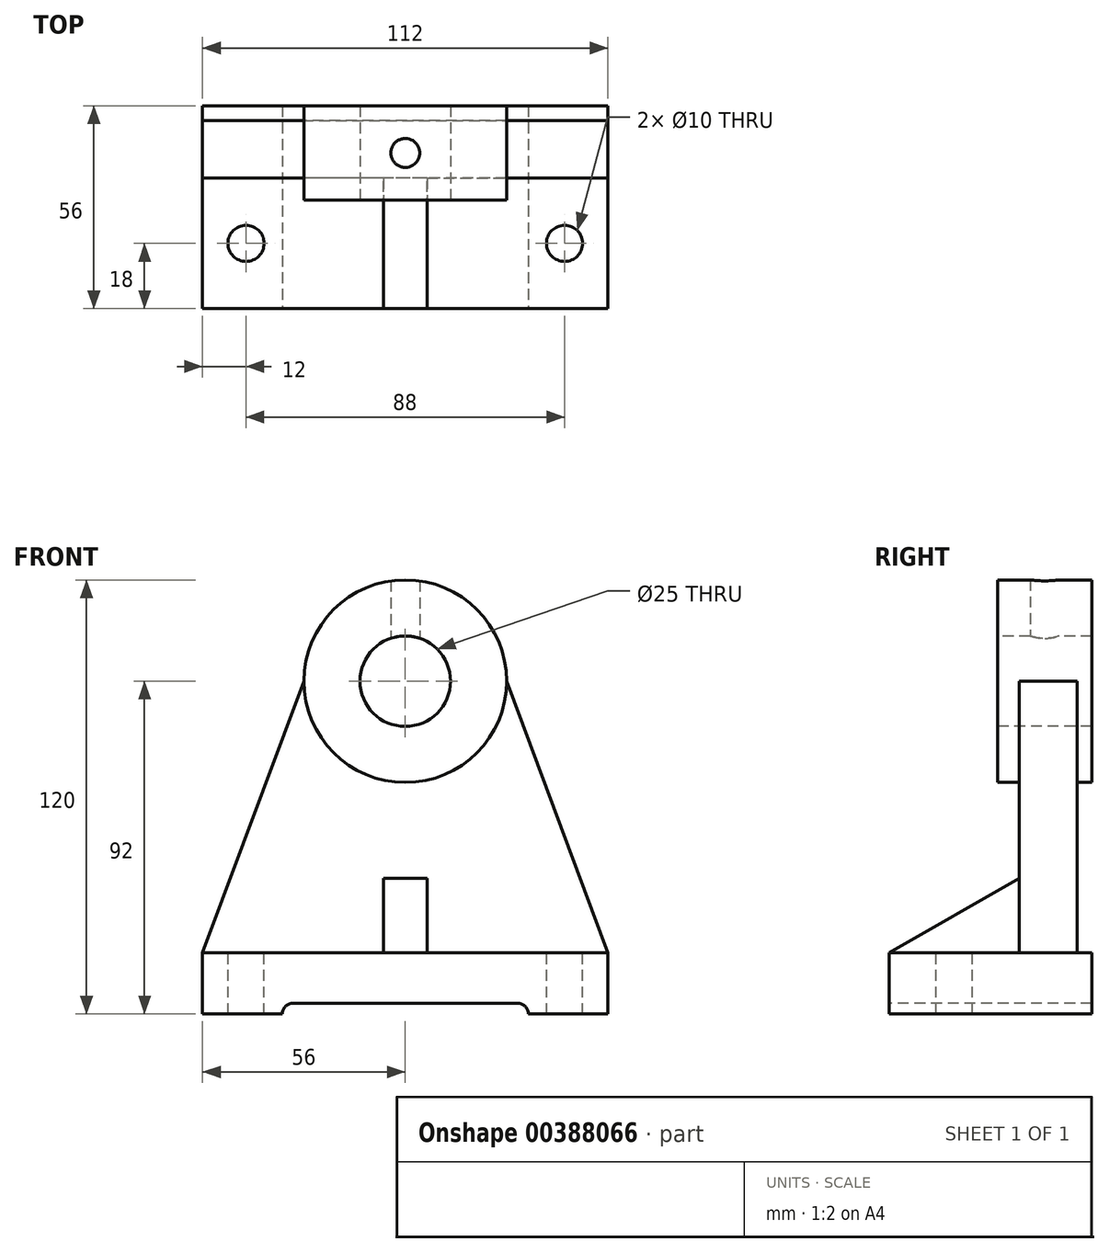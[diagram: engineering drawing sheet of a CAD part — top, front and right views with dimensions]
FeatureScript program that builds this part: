
annotation { "Feature Type Name" : "Feature", "Feature Type Description" : "" }
export const myFeature = defineFeature(function(context is Context, id is Id, definition is map)
    precondition{}
    {
        {
            var Q0;
            Q0=qCreatedBy(makeId("Right.planeOp"),FACE);
            var sketch = newSketch(context, id + "F0", { "sketchPlane" : qUnion([Q0])});
            skLineSegment(sketch, "E0", {"start": v(0, 0) * mm, "end": v(0, 49) * mm});
            skLineSegment(sketch, "E1", {"start": v(0, 0) * mm, "end": v(-56, 0) * mm});
            skLineSegment(sketch, "E2", {"start": v(-56, 0) * mm, "end": v(-56, 17) * mm});
            skLineSegment(sketch, "E3", {"start": v(-20, 37.57) * mm, "end": v(-56, 17) * mm});
            skLineSegment(sketch, "E4", {"start": v(0, 0) * mm, "end": v(0, 92) * mm});
            skLineSegment(sketch, "E5", {"start": v(0, 92) * mm, "end": v(-20, 92) * mm});
            skLineSegment(sketch, "E6", {"start": v(-20, 92) * mm, "end": v(-20, 37.57) * mm});
            skSolve(sketch);
        }
        {
            var Q0;
            Q0 = qSketchRegion(id + "F0", true);
            extrude(context, id + "F1", {"entities" : qUnion([Q0]), "depth" : 112 * mm});
        }
        {
            var Q0;
            Q0=makeQuery(id+"F1.opExtrude","CAP_FACE",FACE,{"disambiguationData":[OSD([sQuery(id+"F0.wireOp",EDGE,"E1"),sQuery(id+"F0.wireOp",EDGE,"E2"),sQuery(id+"F0.wireOp",EDGE,"E3"),sQuery(id+"F0.wireOp",EDGE,"E4"),sQuery(id+"F0.wireOp",EDGE,"E5"),sQuery(id+"F0.wireOp",EDGE,"E6")])],"isStart":false});
            var sketch = newSketch(context, id + "F2", { "sketchPlane" : qUnion([Q0])});
            skPoint(sketch, "E7.start.orphan", {"position": v(0, 17) * mm});
            skLineSegment(sketch, "E8", {"start": v(-4, 17) * mm, "end": v(0, 17) * mm});
            skLineSegment(sketch, "E9", {"start": v(-4, 17) * mm, "end": v(-4, 92) * mm});
            skSolve(sketch);
        }
        {
            var Q0;
            Q0 = qSketchRegion(id + "F2", true);
            var Q1;
            {var subQ0=sQuery(id+"F2.wireOp",EDGE,"E7");Q1=makeQuery(id+"F2.imprint","IMPRINT",FACE,{"disambiguationData":[TD([[makeQuery(id+"F2.imprint","IMPRINT",EDGE,{"derivedFrom":subQ0}),-1.0]])]});}
            var Q2;
            {var subQ0=sQuery(id+"F2.wireOp",EDGE,"E8");Q2=makeQuery(id+"F2.imprint","IMPRINT",FACE,{"disambiguationData":[TD([[makeQuery(id+"F2.imprint","IMPRINT",EDGE,{"derivedFrom":subQ0}),1.0]])]});}
            extrude(context, id + "F3", {"entities" : qUnion([Q0, Q1, Q2]), "operationType" : NewBodyOperationType.REMOVE, "endBound" : BoundingType.THROUGH_ALL, "oppositeDirection" : true, "depth" : 25 * mm});
        }
        {
            var Q0;
            Q0=makeQuery(id+"F1.opExtrude","CAP_FACE",FACE,{"disambiguationData":[OSD([sQuery(id+"F0.wireOp",EDGE,"E1"),sQuery(id+"F0.wireOp",EDGE,"E2"),sQuery(id+"F0.wireOp",EDGE,"E3"),sQuery(id+"F0.wireOp",EDGE,"E4"),sQuery(id+"F0.wireOp",EDGE,"E5"),sQuery(id+"F0.wireOp",EDGE,"E6")])],"isStart":false});
            var sketch = newSketch(context, id + "F4", { "sketchPlane" : qUnion([Q0])});
            skLineSegment(sketch, "E10", {"start": v(-56, 17) * mm, "end": v(-20, 17) * mm});
            skLineSegment(sketch, "E11", {"start": v(-20, 17) * mm, "end": v(-20, 37.57) * mm});
            skSolve(sketch);
        }
        {
            var Q0;
            Q0 = qSketchRegion(id + "F4", true);
            var Q1;
            Q1=makeQuery(id+"F4.imprint","IMPRINT",FACE,{"disambiguationData":[TD([[makeQuery(id+"F4.imprint","IMPRINT",EDGE,{"derivedFrom":sQuery(id+"F4.wireOp",EDGE,"E10")}),1.0]])]});
            extrude(context, id + "F5", {"entities" : qUnion([Q0, Q1]), "operationType" : NewBodyOperationType.REMOVE, "oppositeDirection" : true, "depth" : 50 * mm});
        }
        {
            var Q0;
            Q0=makeQuery(id+"F1.opExtrude","CAP_FACE",FACE,{"disambiguationData":[OSD([sQuery(id+"F0.wireOp",EDGE,"E1"),sQuery(id+"F0.wireOp",EDGE,"E2"),sQuery(id+"F0.wireOp",EDGE,"E3"),sQuery(id+"F0.wireOp",EDGE,"E4"),sQuery(id+"F0.wireOp",EDGE,"E5"),sQuery(id+"F0.wireOp",EDGE,"E6")])],"isStart":true});
            var sketch = newSketch(context, id + "F6", { "sketchPlane" : qUnion([Q0])});
            skLineSegment(sketch, "E12", {"start": v(56, 17) * mm, "end": v(20, 17) * mm});
            skLineSegment(sketch, "E13", {"start": v(20, 17) * mm, "end": v(20, 37.57) * mm});
            skSolve(sketch);
        }
        {
            var Q0;
            Q0 = qSketchRegion(id + "F6", true);
            var Q1;
            Q1=makeQuery(id+"F6.imprint","IMPRINT",FACE,{"disambiguationData":[TD([[makeQuery(id+"F6.imprint","IMPRINT",EDGE,{"derivedFrom":sQuery(id+"F6.wireOp",EDGE,"E12")}),-1.0]])]});
            extrude(context, id + "F7", {"entities" : qUnion([Q0, Q1]), "operationType" : NewBodyOperationType.REMOVE, "oppositeDirection" : true, "depth" : 50 * mm});
        }
        {
            var Q0;
            Q0=makeQuery(id+"F3.boolean.opBoolean","COPY",FACE,{"derivedFrom":makeQuery(id+"F3.opExtrude","SWEPT_FACE",FACE,{"disambiguationData":[OSD([sQuery(id+"F2.wireOp",EDGE,"E9")])]})});
            var sketch = newSketch(context, id + "F8", { "sketchPlane" : qUnion([Q0])});
            skCircle(sketch, "E14", {"center": v(-56, 92) * mm, "radius": 12.5 * mm});
            skCircle(sketch, "E15", {"center": v(-56, 92) * mm, "radius": 28 * mm});
            skLineSegment(sketch, "E16", {"start": v(-28, 92) * mm, "end": v(0, 17) * mm});
            skLineSegment(sketch, "E17", {"start": v(-84, 92) * mm, "end": v(-112, 17) * mm});
            skSolve(sketch);
        }
        {
            var Q0;
            {var subQ0=sQuery(id+"F8.wireOp",EDGE,"E17");Q0=makeQuery(id+"F8.imprint","IMPRINT",FACE,{"disambiguationData":[TD([[makeQuery(id+"F8.imprint","IMPRINT",EDGE,{"derivedFrom":subQ0}),-1.0]])]});}
            var Q1;
            {var subQ0=sQuery(id+"F8.wireOp",EDGE,"E16");Q1=makeQuery(id+"F8.imprint","IMPRINT",FACE,{"disambiguationData":[TD([[makeQuery(id+"F8.imprint","IMPRINT",EDGE,{"derivedFrom":subQ0}),1.0]])]});}
            extrude(context, id + "F9", {"entities" : qUnion([Q0, Q1]), "operationType" : NewBodyOperationType.REMOVE, "oppositeDirection" : true, "depth" : 25 * mm});
        }
        {
            var Q0;
            Q0 = qSketchRegion(id + "F8", true);
            extrude(context, id + "F10", {"entities" : qUnion([Q0]), "operationType" : NewBodyOperationType.ADD, "depth" : 4 * mm, "hasSecondDirection" : true, "secondDirectionOppositeDirection" : true, "secondDirectionDepth" : 22 * mm});
        }
        {
            var Q0;
            Q0=makeQuery(id+"F10.boolean.opBoolean","SPLIT",FACE,{"disambiguationData":[TD([makeQuery(id+"F1.opExtrude","SWEPT_FACE",FACE,{"disambiguationData":[OSD([sQuery(id+"F0.wireOp",EDGE,"E5")])]})])],"derivedFrom":makeQuery(id+"F7.boolean.opBoolean","MERGE",FACE,{"derivedFrom":[makeQuery(id+"F5.boolean.opBoolean","MERGE",FACE,{"derivedFrom":[makeQuery(id+"F1.opExtrude","SWEPT_FACE",FACE,{"disambiguationData":[OSD([sQuery(id+"F0.wireOp",EDGE,"E6")])]}),makeQuery(id+"F5.opExtrude","SWEPT_FACE",FACE,{"disambiguationData":[OSD([sQuery(id+"F4.wireOp",EDGE,"E11")])]})]}),makeQuery(id+"F7.opExtrude","SWEPT_FACE",FACE,{"disambiguationData":[OSD([sQuery(id+"F6.wireOp",EDGE,"E13")])]})]})});
            var sketch = newSketch(context, id + "F11", { "sketchPlane" : qUnion([Q0])});
            skCircle(sketch, "E18", {"center": v(56, 92) * mm, "radius": 12.5 * mm});
            skSolve(sketch);
        }
        {
            var Q0;
            Q0=makeQuery(id+"F1.opExtrude","SWEPT_FACE",FACE,{"disambiguationData":[OSD([sQuery(id+"F0.wireOp",EDGE,"E2")])]});
            var sketch = newSketch(context, id + "F12", { "sketchPlane" : qUnion([Q0])});
            skLineSegment(sketch, "E19", {"start": v(22, 0) * mm, "end": v(22, 3) * mm});
            skLineSegment(sketch, "E20", {"start": v(22, 3) * mm, "end": v(90, 3) * mm});
            skLineSegment(sketch, "E21", {"start": v(90, 3) * mm, "end": v(90, 0) * mm});
            skSolve(sketch);
        }
        {
            var Q0;
            Q0 = qSketchRegion(id + "F12", true);
            var Q1;
            {var subQ0=sQuery(id+"F12.wireOp",EDGE,"E19");Q1=makeQuery(id+"F12.imprint","IMPRINT",FACE,{"disambiguationData":[TD([[makeQuery(id+"F12.imprint","IMPRINT",EDGE,{"derivedFrom":subQ0}),-1.0]])]});}
            extrude(context, id + "F13", {"entities" : qUnion([Q0, Q1]), "operationType" : NewBodyOperationType.REMOVE, "endBound" : BoundingType.THROUGH_ALL, "oppositeDirection" : true, "depth" : 25 * mm});
        }
        {
            var Q0;
            Q0=makeQuery(id+"F7.boolean.opBoolean","COPY",FACE,{"derivedFrom":makeQuery(id+"F7.opExtrude","SWEPT_FACE",FACE,{"disambiguationData":[OSD([sQuery(id+"F6.wireOp",EDGE,"E12")])]})});
            var sketch = newSketch(context, id + "F14", { "sketchPlane" : qUnion([Q0])});
            skCircle(sketch, "E22", {"center": v(12, -38) * mm, "radius": 5 * mm});
            skCircle(sketch, "E23", {"center": v(100, -38) * mm, "radius": 5 * mm});
            skSolve(sketch);
        }
        {
            var Q0;
            Q0 = qSketchRegion(id + "F14", true);
            extrude(context, id + "F15", {"entities" : qUnion([Q0]), "operationType" : NewBodyOperationType.REMOVE, "oppositeDirection" : true, "depth" : 25 * mm});
        }
        {
            var Q0;
            Q0=makeQuery(id+"F13.boolean.opBoolean","COPY",FACE,{"derivedFrom":makeQuery(id+"F13.opExtrude","SWEPT_FACE",FACE,{"disambiguationData":[OSD([sQuery(id+"F12.wireOp",EDGE,"E20")])]})});
            var sketch = newSketch(context, id + "F16", { "sketchPlane" : qUnion([Q0])});
            skCircle(sketch, "E24", {"center": v(56, 13) * mm, "radius": 4 * mm});
            skPoint(sketch, "E24.centerSnap0", {"position": v(56, 0) * mm});
            skSolve(sketch);
        }
        {
            var Q0;
            Q0 = qSketchRegion(id + "F16", true);
            extrude(context, id + "F17", {"entities" : qUnion([Q0]), "operationType" : NewBodyOperationType.REMOVE, "endBound" : BoundingType.THROUGH_ALL, "oppositeDirection" : true, "depth" : 25 * mm});
        }
        {
            var Q0;
            Q0=makeQuery(id+"F13.boolean.opBoolean","COPY",FACE,{"derivedFrom":makeQuery(id+"F13.opExtrude","SWEPT_FACE",FACE,{"disambiguationData":[OSD([sQuery(id+"F12.wireOp",EDGE,"E20")])]})});
            var sketch = newSketch(context, id + "F18", { "sketchPlane" : qUnion([Q0])});
            skCircle(sketch, "E25", {"center": v(56, 13) * mm, "radius": 4 * mm});
            skSolve(sketch);
        }
        {
            var Q0;
            Q0 = qSketchRegion(id + "F18", true);
            extrude(context, id + "F19", {"entities" : qUnion([Q0]), "operationType" : NewBodyOperationType.ADD, "oppositeDirection" : true, "depth" : 80 * mm});
        }
        {
            var Q0;
            Q0 = qSketchRegion(id + "F11", true);
            extrude(context, id + "F20", {"entities" : qUnion([Q0]), "operationType" : NewBodyOperationType.REMOVE, "oppositeDirection" : true, "depth" : 25 * mm, "hasSecondDirection" : true, "secondDirectionOppositeDirection" : false, "secondDirectionDepth" : 25 * mm});
        }
        {
            var Q0;
            Q0=makeQuery(id+"F13.boolean.opBoolean","COPY",EDGE,{"derivedFrom":makeQuery(id+"F13.opExtrude","SWEPT_EDGE",EDGE,{"disambiguationData":[OSD([sQuery(id+"F12.wireOp",EDGE,"E19"),sQuery(id+"F12.wireOp",EDGE,"E20")])]})});
            var Q1;
            Q1=makeQuery(id+"F13.boolean.opBoolean","COPY",EDGE,{"derivedFrom":makeQuery(id+"F13.opExtrude","SWEPT_EDGE",EDGE,{"disambiguationData":[OSD([sQuery(id+"F12.wireOp",EDGE,"E20"),sQuery(id+"F12.wireOp",EDGE,"E21")])]})});
            fillet(context, id + "F21", {"entities" : qUnion([Q0, Q1]), "radius" : 3 * mm, "tangentPropagation" : true, "allowEdgeOverflow" : false});
        }
    });
